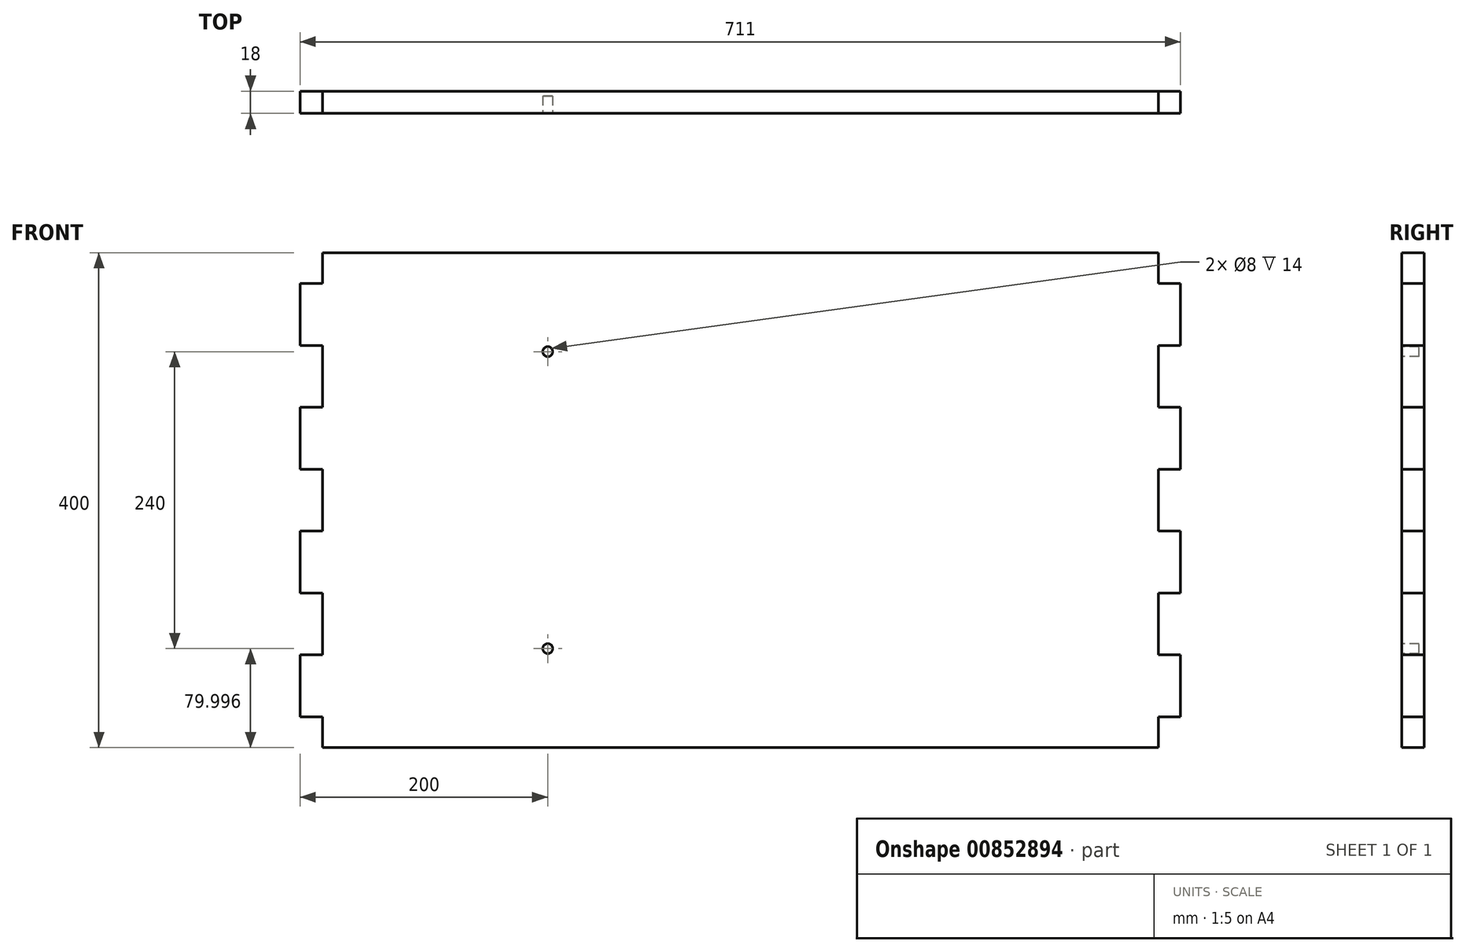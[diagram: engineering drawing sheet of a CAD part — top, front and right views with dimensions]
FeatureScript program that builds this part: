
annotation { "Feature Type Name" : "Feature", "Feature Type Description" : "" }
export const myFeature = defineFeature(function(context is Context, id is Id, definition is map)
    precondition{}
    {
        {
            var Q0;
            Q0=qCreatedBy(makeId("Front.planeOp"),FACE);
            var sketch = newSketch(context, id + "F0", { "sketchPlane" : qUnion([Q0])});
            skPoint(sketch, "E0.middle", {"position": v(0, 0) * mm});
            skLineSegment(sketch, "E1", {"start": v(-337.5, 194.2) * mm, "end": v(337.5, 194.2) * mm});
            skLineSegment(sketch, "E2", {"start": v(-337.5, -205.8) * mm, "end": v(337.5, -205.8) * mm});
            skLineSegment(sketch, "E3", {"start": v(337.5, 194.2) * mm, "end": v(337.5, 169.2) * mm});
            skLineSegment(sketch, "E4", {"start": v(337.5, 169.2) * mm, "end": v(355.5, 169.2) * mm});
            skLineSegment(sketch, "E5", {"start": v(355.5, 169.2) * mm, "end": v(355.5, 119.2) * mm});
            skLineSegment(sketch, "E6", {"start": v(355.5, 119.2) * mm, "end": v(337.5, 119.2) * mm});
            skLineSegment(sketch, "E7", {"start": v(337.5, 119.2) * mm, "end": v(337.5, 69.2) * mm});
            skLineSegment(sketch, "E8", {"start": v(337.5, 69.2) * mm, "end": v(355.5, 69.2) * mm});
            skLineSegment(sketch, "E9", {"start": v(355.5, 69.2) * mm, "end": v(355.5, 19.2) * mm});
            skLineSegment(sketch, "E10", {"start": v(355.5, 19.2) * mm, "end": v(337.5, 19.2) * mm});
            skLineSegment(sketch, "E11", {"start": v(337.5, 19.2) * mm, "end": v(337.5, -30.8) * mm});
            skLineSegment(sketch, "E12", {"start": v(337.5, -30.8) * mm, "end": v(355.5, -30.8) * mm});
            skLineSegment(sketch, "E13", {"start": v(355.5, -30.8) * mm, "end": v(355.5, -80.8) * mm});
            skLineSegment(sketch, "E14", {"start": v(355.5, -80.8) * mm, "end": v(337.5, -80.8) * mm});
            skLineSegment(sketch, "E15", {"start": v(337.5, -80.8) * mm, "end": v(337.5, -130.8) * mm});
            skLineSegment(sketch, "E16", {"start": v(337.5, -130.8) * mm, "end": v(355.5, -130.8) * mm});
            skLineSegment(sketch, "E17", {"start": v(355.5, -130.8) * mm, "end": v(355.5, -180.8) * mm});
            skLineSegment(sketch, "E18", {"start": v(355.5, -180.8) * mm, "end": v(337.5, -180.8) * mm});
            skLineSegment(sketch, "E19", {"start": v(337.5, -180.8) * mm, "end": v(337.5, -205.8) * mm});
            skLineSegment(sketch, "E20.MirrorCS", {"start": v(-355.5, -80.8) * mm, "end": v(-337.5, -80.8) * mm});
            skLineSegment(sketch, "E21.MirrorCS", {"start": v(-355.5, -180.8) * mm, "end": v(-337.5, -180.8) * mm});
            skLineSegment(sketch, "E22.MirrorCS", {"start": v(-337.5, -130.8) * mm, "end": v(-355.5, -130.8) * mm});
            skLineSegment(sketch, "E23.MirrorCS", {"start": v(-337.5, -30.8) * mm, "end": v(-355.5, -30.8) * mm});
            skLineSegment(sketch, "E24.MirrorCS", {"start": v(-355.5, -130.8) * mm, "end": v(-355.5, -180.8) * mm});
            skLineSegment(sketch, "E25.MirrorCS", {"start": v(-337.5, 169.2) * mm, "end": v(-355.5, 169.2) * mm});
            skLineSegment(sketch, "E26.MirrorCS", {"start": v(-355.5, 69.2) * mm, "end": v(-355.5, 19.2) * mm});
            skLineSegment(sketch, "E27.MirrorCS", {"start": v(-355.5, 119.2) * mm, "end": v(-337.5, 119.2) * mm});
            skLineSegment(sketch, "E28.MirrorCS", {"start": v(-337.5, -80.8) * mm, "end": v(-337.5, -130.8) * mm});
            skLineSegment(sketch, "E29.MirrorCS", {"start": v(-337.5, 69.2) * mm, "end": v(-355.5, 69.2) * mm});
            skLineSegment(sketch, "E30.MirrorCS", {"start": v(-337.5, 19.2) * mm, "end": v(-337.5, -30.8) * mm});
            skLineSegment(sketch, "E31.MirrorCS", {"start": v(-337.5, 119.2) * mm, "end": v(-337.5, 69.2) * mm});
            skLineSegment(sketch, "E32.MirrorCS", {"start": v(-355.5, 169.2) * mm, "end": v(-355.5, 119.2) * mm});
            skLineSegment(sketch, "E33.MirrorCS", {"start": v(-355.5, 19.2) * mm, "end": v(-337.5, 19.2) * mm});
            skLineSegment(sketch, "E34.MirrorCS", {"start": v(-355.5, -30.8) * mm, "end": v(-355.5, -80.8) * mm});
            skLineSegment(sketch, "E35", {"start": v(-337.5, 194.2) * mm, "end": v(-337.5, 169.2) * mm});
            skLineSegment(sketch, "E36", {"start": v(-337.5, -180.8) * mm, "end": v(-337.5, -205.8) * mm});
            skSolve(sketch);
        }
        {
            var Q0;
            Q0=makeQuery(id+"F0.imprint","IMPRINT",FACE,{"disambiguationData":[TD([[makeQuery(id+"F0.imprint","IMPRINT",EDGE,{"derivedFrom":sQuery(id+"F0.wireOp",EDGE,"E1")}),-1.0]])]});
            extrude(context, id + "F1", {"entities" : qUnion([Q0]), "depth" : 18 * mm, "offsetDistance" : 25 * mm});
        }
        {
            var Q0;
            Q0=makeQuery(id+"F1.opExtrude","CAP_FACE",FACE,{"disambiguationData":[OSD([sQuery(id+"F0.wireOp",EDGE,"E1"),sQuery(id+"F0.wireOp",EDGE,"E2"),sQuery(id+"F0.wireOp",EDGE,"ewyYqhio-DAJe-XwCx-cMG6-GK5fvQsuxPU7"),sQuery(id+"F0.wireOp",EDGE,"nHFftgDy-i5YC-rqQy-M2vt-WPnWGVSwTjn5"),sQuery(id+"F0.wireOp",EDGE,"z4BhC4GM-opnc-4T81-oUF8-uJKcAJ8t9Wc0"),sQuery(id+"F0.wireOp",EDGE,"tSiJu8Kq-1KbO-zGV1-f4Kd-irEQgRFnsvFi"),sQuery(id+"F0.wireOp",EDGE,"bnhhpTOf-VStw-dUyz-0Sey-UxC9XC9HOaeJ"),sQuery(id+"F0.wireOp",EDGE,"hYWqMa1f-J4mn-HBe6-ceax-sLWvmMLqbbz1"),sQuery(id+"F0.wireOp",EDGE,"VcTMG8FJ-Fp5Y-PNPF-9lYJ-ioq4plAh1D12"),sQuery(id+"F0.wireOp",EDGE,"f3F1PxdX-O6lW-EGjf-Lmp5-zxO7BYcBg0e8"),sQuery(id+"F0.wireOp",EDGE,"tm3tiRFD-xuHA-kPII-pd0Y-N0IUgJs61i0C"),sQuery(id+"F0.wireOp",EDGE,"CNwAosah-Vem8-Qc4F-CnMj-YLP0e1ON6FDJ"),sQuery(id+"F0.wireOp",EDGE,"siwTUR6W-f5gS-RNm4-v4lg-xR03EECh1xZg"),sQuery(id+"F0.wireOp",EDGE,"DaDnjV5b-wAJr-b3Op-lsnt-LNOT2o912iCd"),sQuery(id+"F0.wireOp",EDGE,"opgCK299-jtlf-LOyB-yDxD-ObXlQyzkbD1J"),sQuery(id+"F0.wireOp",EDGE,"HuJ8HwzE-lFcn-RtkN-7d6Z-VouE9wEQK545"),sQuery(id+"F0.wireOp",EDGE,"HpaP9hMo-YQKa-7RMg-F70R-QrUY8arBLz43"),sQuery(id+"F0.wireOp",EDGE,"zism0PR5-nTsj-JiCQ-Cn6K-UoHpQQI1j2u7"),sQuery(id+"F0.wireOp",EDGE,"fQbVAuh3-2b5f-YIxg-pHJ1-xPp372vZBIEJ"),sQuery(id+"F0.wireOp",EDGE,"5b457bac-05f0-4ebd-b4a5-5844c1aeaf6d0.MirrorCS"),sQuery(id+"F0.wireOp",EDGE,"5b457bac-05f0-4ebd-b4a5-5844c1aeaf6d1.MirrorCS"),sQuery(id+"F0.wireOp",EDGE,"5b457bac-05f0-4ebd-b4a5-5844c1aeaf6d2.MirrorCS"),sQuery(id+"F0.wireOp",EDGE,"5b457bac-05f0-4ebd-b4a5-5844c1aeaf6d3.MirrorCS"),sQuery(id+"F0.wireOp",EDGE,"5b457bac-05f0-4ebd-b4a5-5844c1aeaf6d4.MirrorCS"),sQuery(id+"F0.wireOp",EDGE,"5b457bac-05f0-4ebd-b4a5-5844c1aeaf6d5.MirrorCS"),sQuery(id+"F0.wireOp",EDGE,"5b457bac-05f0-4ebd-b4a5-5844c1aeaf6d6.MirrorCS"),sQuery(id+"F0.wireOp",EDGE,"5b457bac-05f0-4ebd-b4a5-5844c1aeaf6d7.MirrorCS"),sQuery(id+"F0.wireOp",EDGE,"5b457bac-05f0-4ebd-b4a5-5844c1aeaf6d8.MirrorCS"),sQuery(id+"F0.wireOp",EDGE,"5b457bac-05f0-4ebd-b4a5-5844c1aeaf6d9.MirrorCS"),sQuery(id+"F0.wireOp",EDGE,"5b457bac-05f0-4ebd-b4a5-5844c1aeaf6d10.MirrorCS"),sQuery(id+"F0.wireOp",EDGE,"5b457bac-05f0-4ebd-b4a5-5844c1aeaf6d11.MirrorCS"),sQuery(id+"F0.wireOp",EDGE,"5b457bac-05f0-4ebd-b4a5-5844c1aeaf6d12.MirrorCS"),sQuery(id+"F0.wireOp",EDGE,"5b457bac-05f0-4ebd-b4a5-5844c1aeaf6d13.MirrorCS"),sQuery(id+"F0.wireOp",EDGE,"5b457bac-05f0-4ebd-b4a5-5844c1aeaf6d14.MirrorCS"),sQuery(id+"F0.wireOp",EDGE,"DmvNAE1j-j7So-Rx0h-tLjE-8Ha2XCa4Yq4L"),sQuery(id+"F0.wireOp",EDGE,"zPvEcsUZ-aCOx-KKB8-QoCm-7Z1M2p1nImxw")])],"isStart":false});
            var sketch = newSketch(context, id + "F2", { "sketchPlane" : qUnion([Q0])});
            skCircle(sketch, "E37", {"center": v(-155.5, 114.2) * mm, "radius": 4 * mm});
            skCircle(sketch, "E38", {"center": v(-155.5, -125.8) * mm, "radius": 4 * mm});
            skSolve(sketch);
        }
        {
            var Q0;
            Q0=makeQuery(id+"F2.imprint","IMPRINT",FACE,{"disambiguationData":[TD([[makeQuery(id+"F2.imprint","IMPRINT",EDGE,{"derivedFrom":sQuery(id+"F2.wireOp",EDGE,"E38")}),1.0]])]});
            var Q1;
            Q1=makeQuery(id+"F2.imprint","IMPRINT",FACE,{"disambiguationData":[TD([[makeQuery(id+"F2.imprint","IMPRINT",EDGE,{"derivedFrom":sQuery(id+"F2.wireOp",EDGE,"E37")}),1.0]])]});
            extrude(context, id + "F3", {"entities" : qUnion([Q0, Q1]), "operationType" : NewBodyOperationType.REMOVE, "oppositeDirection" : true, "depth" : 14 * mm, "offsetDistance" : 25 * mm});
        }
    });
